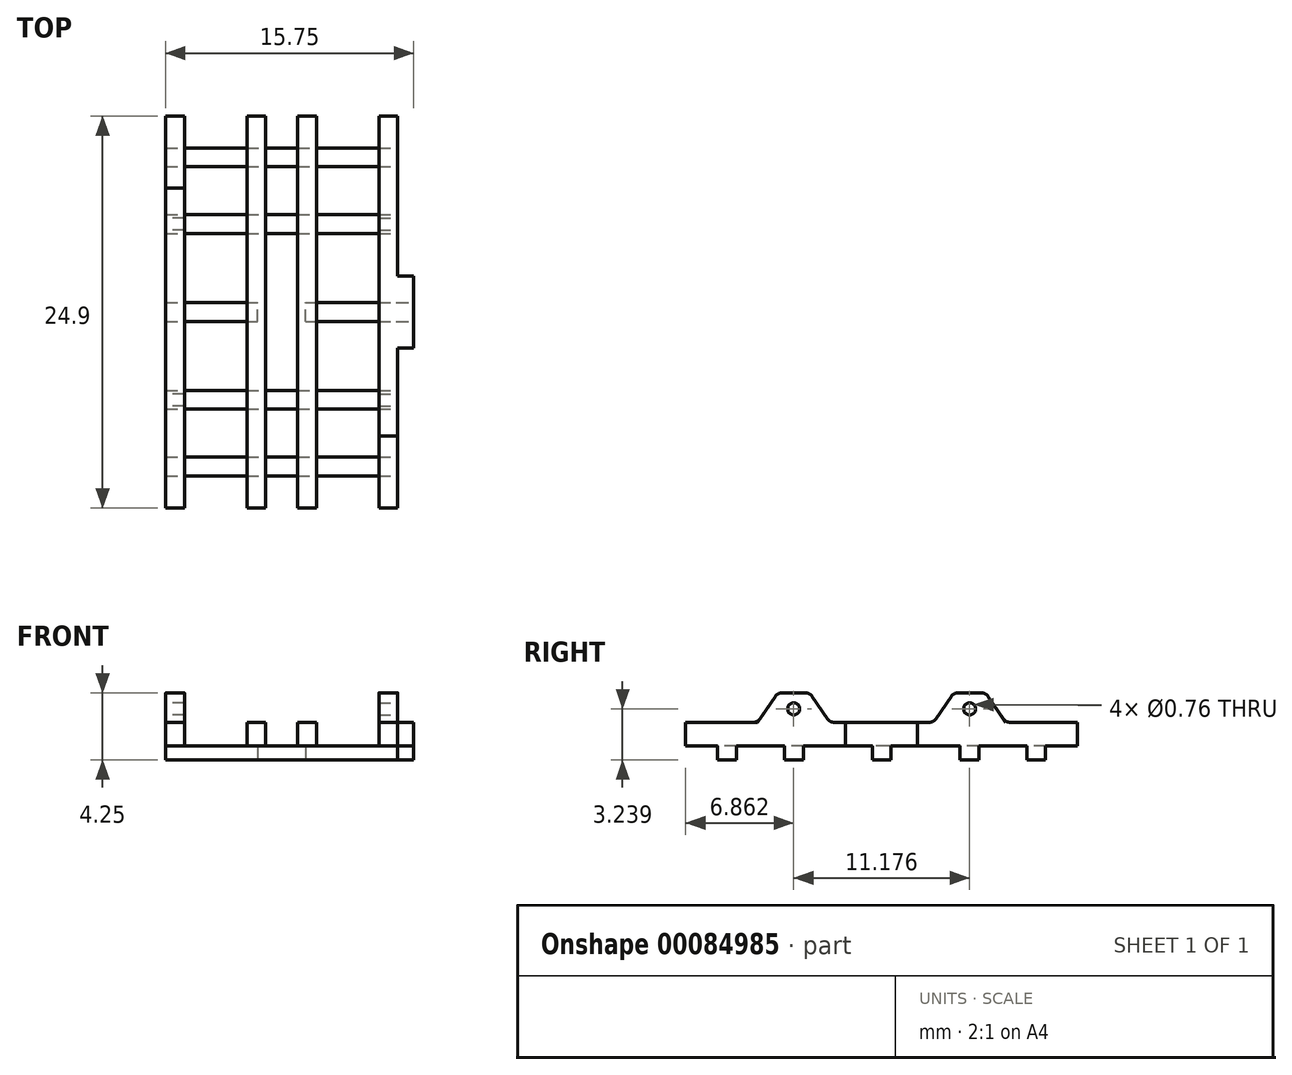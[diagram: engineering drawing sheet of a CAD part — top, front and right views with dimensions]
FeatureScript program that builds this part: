
annotation { "Feature Type Name" : "Feature", "Feature Type Description" : "" }
export const myFeature = defineFeature(function(context is Context, id is Id, definition is map)
    precondition{}
    {
        {
            var Q0;
            Q0=qCreatedBy(makeId("Top.planeOp"),FACE);
            var sketch = newSketch(context, id + "F0", { "sketchPlane" : qUnion([Q0])});
            skLineSegment(sketch, "E0.bottom", {"start": v(-7.37, 10.41) * mm, "end": v(7.37, 10.41) * mm});
            skLineSegment(sketch, "E0.top", {"start": v(-7.37, -10.41) * mm, "end": v(7.37, -10.41) * mm});
            skLineSegment(sketch, "E0.left", {"start": v(-7.37, 10.41) * mm, "end": v(-7.37, 9.22) * mm});
            skLineSegment(sketch, "E0.right", {"start": v(7.37, 10.41) * mm, "end": v(7.37, 9.22) * mm});
            skLineSegment(sketch, "E1", {"start": v(-7.37, 9.22) * mm, "end": v(7.37, 9.22) * mm});
            skLineSegment(sketch, "E2", {"start": v(-7.37, -9.22) * mm, "end": v(7.37, -9.22) * mm});
            skLineSegment(sketch, "E3", {"start": v(-7.37, -6.17) * mm, "end": v(7.37, -6.17) * mm});
            skLineSegment(sketch, "E4", {"start": v(-7.37, -4.98) * mm, "end": v(7.37, -4.98) * mm});
            skLineSegment(sketch, "E5", {"start": v(-7.37, -0.6) * mm, "end": v(7.37, -0.6) * mm});
            skLineSegment(sketch, "E6", {"start": v(-7.37, 0.6) * mm, "end": v(7.37, 0.6) * mm});
            skLineSegment(sketch, "E7", {"start": v(-7.37, 6.17) * mm, "end": v(7.37, 6.17) * mm});
            skLineSegment(sketch, "E8", {"start": v(-7.37, 4.98) * mm, "end": v(7.37, 4.98) * mm});
            skLineSegment(sketch, "E9.trimOffspring", {"start": v(-7.37, 6.17) * mm, "end": v(-7.37, 4.98) * mm});
            skLineSegment(sketch, "E10.trimOffspring", {"start": v(7.37, 6.17) * mm, "end": v(7.37, 4.98) * mm});
            skLineSegment(sketch, "E11.trimOffspring", {"start": v(-7.37, 0.6) * mm, "end": v(-7.37, -0.6) * mm});
            skLineSegment(sketch, "E12.trimOffspring", {"start": v(7.37, 0.6) * mm, "end": v(7.37, -0.6) * mm});
            skLineSegment(sketch, "E13.trimOffspring", {"start": v(-7.37, -4.98) * mm, "end": v(-7.37, -6.17) * mm});
            skLineSegment(sketch, "E14.trimOffspring", {"start": v(7.37, -4.98) * mm, "end": v(7.37, -6.17) * mm});
            skLineSegment(sketch, "E15.trimOffspring", {"start": v(7.37, -9.22) * mm, "end": v(7.37, -10.41) * mm});
            skLineSegment(sketch, "E16.trimOffspring", {"start": v(-7.37, -9.22) * mm, "end": v(-7.37, -10.41) * mm});
            skSolve(sketch);
        }
        {
            var Q0;
            Q0 = qSketchRegion(id + "F0", true);
            extrude(context, id + "F1", {"entities" : qUnion([Q0]), "depth" : 0.89 * mm});
        }
        {
            var Q0;
            Q0=makeQuery(id+"F1.opExtrude","CAP_FACE",FACE,{"disambiguationData":[OSD([sQuery(id+"F0.wireOp",EDGE,"E0.bottom"),sQuery(id+"F0.wireOp",EDGE,"E0.left"),sQuery(id+"F0.wireOp",EDGE,"E0.right"),sQuery(id+"F0.wireOp",EDGE,"E1")])],"isStart":false});
            var sketch = newSketch(context, id + "F2", { "sketchPlane" : qUnion([Q0])});
            skLineSegment(sketch, "E17.bottom", {"start": v(-7.37, 12.45) * mm, "end": v(-6.17, 12.45) * mm});
            skLineSegment(sketch, "E17.top", {"start": v(-7.37, -12.45) * mm, "end": v(-6.17, -12.45) * mm});
            skLineSegment(sketch, "E17.left", {"start": v(-7.37, 12.45) * mm, "end": v(-7.37, -12.45) * mm});
            skLineSegment(sketch, "E17.right", {"start": v(-6.17, 12.45) * mm, "end": v(-6.17, -12.45) * mm});
            skLineSegment(sketch, "E18.bottom", {"start": v(7.37, 12.45) * mm, "end": v(6.17, 12.45) * mm});
            skLineSegment(sketch, "E18.top", {"start": v(7.37, -12.45) * mm, "end": v(6.17, -12.45) * mm});
            skLineSegment(sketch, "E18.left", {"start": v(7.37, 12.45) * mm, "end": v(7.37, -12.45) * mm});
            skLineSegment(sketch, "E18.right", {"start": v(6.17, 12.45) * mm, "end": v(6.17, -12.45) * mm});
            skLineSegment(sketch, "E19.bottom", {"start": v(-2.2, 12.45) * mm, "end": v(-1.02, 12.45) * mm});
            skLineSegment(sketch, "E19.top", {"start": v(-2.2, -12.45) * mm, "end": v(-1.02, -12.45) * mm});
            skLineSegment(sketch, "E19.left", {"start": v(-2.2, 12.45) * mm, "end": v(-2.2, -12.45) * mm});
            skLineSegment(sketch, "E19.right", {"start": v(-1.02, 12.45) * mm, "end": v(-1.02, -12.45) * mm});
            skLineSegment(sketch, "E20.bottom", {"start": v(1.02, 12.45) * mm, "end": v(2.2, 12.45) * mm});
            skLineSegment(sketch, "E20.top", {"start": v(1.02, -12.45) * mm, "end": v(2.2, -12.45) * mm});
            skLineSegment(sketch, "E20.left", {"start": v(1.02, 12.45) * mm, "end": v(1.02, -12.45) * mm});
            skLineSegment(sketch, "E20.right", {"start": v(2.2, 12.45) * mm, "end": v(2.2, -12.45) * mm});
            skSolve(sketch);
        }
        {
            var Q0;
            Q0 = qSketchRegion(id + "F2", true);
            extrude(context, id + "F3", {"entities" : qUnion([Q0]), "operationType" : NewBodyOperationType.ADD, "depth" : 1.5 * mm});
        }
        {
            var Q0;
            Q0=makeQuery(id+"F3.boolean.opBoolean","MERGE",FACE,{"derivedFrom":[makeQuery(id+"F1.opExtrude","SWEPT_FACE",FACE,{"disambiguationData":[OSD([sQuery(id+"F0.wireOp",EDGE,"E0.left")])]}),makeQuery(id+"F1.opExtrude","SWEPT_FACE",FACE,{"disambiguationData":[OSD([sQuery(id+"F0.wireOp",EDGE,"E9.trimOffspring")])]}),makeQuery(id+"F1.opExtrude","SWEPT_FACE",FACE,{"disambiguationData":[OSD([sQuery(id+"F0.wireOp",EDGE,"E11.trimOffspring")])]}),makeQuery(id+"F1.opExtrude","SWEPT_FACE",FACE,{"disambiguationData":[OSD([sQuery(id+"F0.wireOp",EDGE,"E13.trimOffspring")])]}),makeQuery(id+"F1.opExtrude","SWEPT_FACE",FACE,{"disambiguationData":[OSD([sQuery(id+"F0.wireOp",EDGE,"E16.trimOffspring")])]}),makeQuery(id+"F3.opExtrude","SWEPT_FACE",FACE,{"disambiguationData":[OSD([sQuery(id+"F2.wireOp",EDGE,"E17.left")])]})]});
            var sketch = newSketch(context, id + "F4", { "sketchPlane" : qUnion([Q0])});
            skLineSegment(sketch, "E21", {"start": v(-7.87, 2.39) * mm, "end": v(-6.6, 4.25) * mm});
            skLineSegment(sketch, "E22", {"start": v(-6.6, 4.25) * mm, "end": v(-4.57, 4.25) * mm});
            skLineSegment(sketch, "E23", {"start": v(-4.57, 4.25) * mm, "end": v(-3.3, 2.39) * mm});
            skLineSegment(sketch, "E24", {"start": v(-3.3, 2.39) * mm, "end": v(-7.87, 2.39) * mm});
            skCircle(sketch, "E25", {"center": v(-5.59, 3.24) * mm, "radius": 0.38 * mm});
            skPoint(sketch, "E25.centerSnap0", {"position": v(-5.59, 4.25) * mm});
            skLineSegment(sketch, "E26.MirrorCS", {"start": v(3.3, 2.39) * mm, "end": v(7.87, 2.39) * mm});
            skLineSegment(sketch, "E27.MirrorCS", {"start": v(4.57, 4.25) * mm, "end": v(3.3, 2.39) * mm});
            skCircle(sketch, "E28.MirrorC", {"center": v(5.59, 3.24) * mm, "radius": 0.38 * mm});
            skLineSegment(sketch, "E29.MirrorCS", {"start": v(6.6, 4.25) * mm, "end": v(4.57, 4.25) * mm});
            skPoint(sketch, "E30.MirrorP", {"position": v(5.59, 4.25) * mm});
            skLineSegment(sketch, "E31.MirrorCS", {"start": v(7.87, 2.39) * mm, "end": v(6.6, 4.25) * mm});
            skSolve(sketch);
        }
        {
            var Q0;
            Q0 = qSketchRegion(id + "F4", true);
            extrude(context, id + "F5", {"entities" : qUnion([Q0]), "operationType" : NewBodyOperationType.ADD, "oppositeDirection" : true, "depth" : 1.2 * mm});
        }
        {
            var Q0;
            Q0=makeQuery(id+"F3.boolean.opBoolean","MERGE",FACE,{"derivedFrom":[makeQuery(id+"F1.opExtrude","SWEPT_FACE",FACE,{"disambiguationData":[OSD([sQuery(id+"F0.wireOp",EDGE,"E0.right")])]}),makeQuery(id+"F1.opExtrude","SWEPT_FACE",FACE,{"disambiguationData":[OSD([sQuery(id+"F0.wireOp",EDGE,"E10.trimOffspring")])]}),makeQuery(id+"F1.opExtrude","SWEPT_FACE",FACE,{"disambiguationData":[OSD([sQuery(id+"F0.wireOp",EDGE,"E12.trimOffspring")])]}),makeQuery(id+"F1.opExtrude","SWEPT_FACE",FACE,{"disambiguationData":[OSD([sQuery(id+"F0.wireOp",EDGE,"E14.trimOffspring")])]}),makeQuery(id+"F1.opExtrude","SWEPT_FACE",FACE,{"disambiguationData":[OSD([sQuery(id+"F0.wireOp",EDGE,"E15.trimOffspring")])]}),makeQuery(id+"F3.opExtrude","SWEPT_FACE",FACE,{"disambiguationData":[OSD([sQuery(id+"F2.wireOp",EDGE,"E18.left")])]})]});
            var sketch = newSketch(context, id + "F6", { "sketchPlane" : qUnion([Q0])});
            skLineSegment(sketch, "E32", {"start": v(-7.87, 2.39) * mm, "end": v(-3.3, 2.39) * mm});
            skLineSegment(sketch, "E33", {"start": v(-3.3, 2.39) * mm, "end": v(-4.57, 4.25) * mm});
            skLineSegment(sketch, "E34", {"start": v(-4.57, 4.25) * mm, "end": v(-6.6, 4.25) * mm});
            skLineSegment(sketch, "E35", {"start": v(-6.6, 4.25) * mm, "end": v(-7.87, 2.39) * mm});
            skCircle(sketch, "E36", {"center": v(-5.59, 3.24) * mm, "radius": 0.38 * mm});
            skLineSegment(sketch, "E37.MirrorCS", {"start": v(7.87, 2.39) * mm, "end": v(3.3, 2.39) * mm});
            skLineSegment(sketch, "E38.MirrorCS", {"start": v(3.3, 2.39) * mm, "end": v(4.57, 4.25) * mm});
            skLineSegment(sketch, "E39.MirrorCS", {"start": v(4.57, 4.25) * mm, "end": v(6.6, 4.25) * mm});
            skCircle(sketch, "E40.MirrorC", {"center": v(5.59, 3.24) * mm, "radius": 0.38 * mm});
            skLineSegment(sketch, "E41.MirrorCS", {"start": v(6.6, 4.25) * mm, "end": v(7.87, 2.39) * mm});
            skSolve(sketch);
        }
        {
            var Q0;
            Q0 = qSketchRegion(id + "F6", true);
            extrude(context, id + "F7", {"entities" : qUnion([Q0]), "operationType" : NewBodyOperationType.ADD, "oppositeDirection" : true, "depth" : 1.2 * mm});
        }
        {
            var Q0;
            Q0=makeQuery(id+"F7.opExtrude","SWEPT_EDGE",EDGE,{"disambiguationData":[OSD([sQuery(id+"F6.wireOp",EDGE,"E33"),sQuery(id+"F6.wireOp",EDGE,"E34")])]});
            var Q1;
            Q1=makeQuery(id+"F7.opExtrude","SWEPT_EDGE",EDGE,{"disambiguationData":[OSD([sQuery(id+"F6.wireOp",EDGE,"E34"),sQuery(id+"F6.wireOp",EDGE,"E35")])]});
            var Q2;
            Q2=makeQuery(id+"F7.opExtrude","SWEPT_EDGE",EDGE,{"disambiguationData":[OSD([sQuery(id+"F2.wireOp",EDGE,"E18.left"),sQuery(id+"F6.wireOp",EDGE,"E32"),sQuery(id+"F6.wireOp",EDGE,"E33")])]});
            var Q3;
            Q3=makeQuery(id+"F7.opExtrude","SWEPT_EDGE",EDGE,{"disambiguationData":[OSD([sQuery(id+"F2.wireOp",EDGE,"E18.left"),sQuery(id+"F6.wireOp",EDGE,"E32"),sQuery(id+"F6.wireOp",EDGE,"E35")])]});
            var Q4;
            Q4=makeQuery(id+"F7.opExtrude","SWEPT_EDGE",EDGE,{"disambiguationData":[OSD([sQuery(id+"F6.wireOp",EDGE,"E38.MirrorCS"),sQuery(id+"F6.wireOp",EDGE,"E39.MirrorCS")])]});
            var Q5;
            Q5=makeQuery(id+"F7.opExtrude","SWEPT_EDGE",EDGE,{"disambiguationData":[OSD([sQuery(id+"F2.wireOp",EDGE,"E18.left"),sQuery(id+"F6.wireOp",EDGE,"E37.MirrorCS"),sQuery(id+"F6.wireOp",EDGE,"E38.MirrorCS")])]});
            var Q6;
            Q6=makeQuery(id+"F7.opExtrude","SWEPT_EDGE",EDGE,{"disambiguationData":[OSD([sQuery(id+"F6.wireOp",EDGE,"E39.MirrorCS"),sQuery(id+"F6.wireOp",EDGE,"E41.MirrorCS")])]});
            var Q7;
            Q7=makeQuery(id+"F7.opExtrude","SWEPT_EDGE",EDGE,{"disambiguationData":[OSD([sQuery(id+"F2.wireOp",EDGE,"E18.left"),sQuery(id+"F6.wireOp",EDGE,"E37.MirrorCS"),sQuery(id+"F6.wireOp",EDGE,"E41.MirrorCS")])]});
            var Q8;
            Q8=makeQuery(id+"F5.opExtrude","SWEPT_EDGE",EDGE,{"disambiguationData":[OSD([sQuery(id+"F2.wireOp",EDGE,"E17.left"),sQuery(id+"F4.wireOp",EDGE,"E21"),sQuery(id+"F4.wireOp",EDGE,"E24")])]});
            var Q9;
            Q9=makeQuery(id+"F5.opExtrude","SWEPT_EDGE",EDGE,{"disambiguationData":[OSD([sQuery(id+"F4.wireOp",EDGE,"E21"),sQuery(id+"F4.wireOp",EDGE,"E22")])]});
            var Q10;
            Q10=makeQuery(id+"F5.opExtrude","SWEPT_EDGE",EDGE,{"disambiguationData":[OSD([sQuery(id+"F4.wireOp",EDGE,"E22"),sQuery(id+"F4.wireOp",EDGE,"E23")])]});
            var Q11;
            Q11=makeQuery(id+"F5.opExtrude","SWEPT_EDGE",EDGE,{"disambiguationData":[OSD([sQuery(id+"F2.wireOp",EDGE,"E17.left"),sQuery(id+"F4.wireOp",EDGE,"E23"),sQuery(id+"F4.wireOp",EDGE,"E24")])]});
            var Q12;
            Q12=makeQuery(id+"F5.opExtrude","SWEPT_EDGE",EDGE,{"disambiguationData":[OSD([sQuery(id+"F2.wireOp",EDGE,"E17.left"),sQuery(id+"F4.wireOp",EDGE,"E26.MirrorCS"),sQuery(id+"F4.wireOp",EDGE,"E31.MirrorCS")])]});
            var Q13;
            Q13=makeQuery(id+"F5.opExtrude","SWEPT_EDGE",EDGE,{"disambiguationData":[OSD([sQuery(id+"F4.wireOp",EDGE,"E29.MirrorCS"),sQuery(id+"F4.wireOp",EDGE,"E31.MirrorCS")])]});
            var Q14;
            Q14=makeQuery(id+"F5.opExtrude","SWEPT_EDGE",EDGE,{"disambiguationData":[OSD([sQuery(id+"F4.wireOp",EDGE,"E27.MirrorCS"),sQuery(id+"F4.wireOp",EDGE,"E29.MirrorCS")])]});
            var Q15;
            Q15=makeQuery(id+"F5.opExtrude","SWEPT_EDGE",EDGE,{"disambiguationData":[OSD([sQuery(id+"F2.wireOp",EDGE,"E17.left"),sQuery(id+"F4.wireOp",EDGE,"E26.MirrorCS"),sQuery(id+"F4.wireOp",EDGE,"E27.MirrorCS")])]});
            fillet(context, id + "F8", {"entities" : qUnion([Q0, Q1, Q2, Q3, Q4, Q5, Q6, Q7, Q8, Q9, Q10, Q11, Q12, Q13, Q14, Q15]), "radius" : 0.5 * mm, "tangentPropagation" : true, "allowEdgeOverflow" : false});
        }
        {
            var Q0;
            Q0=makeQuery(id+"F1.opExtrude","CAP_FACE",FACE,{"disambiguationData":[OSD([sQuery(id+"F0.wireOp",EDGE,"E5"),sQuery(id+"F0.wireOp",EDGE,"E6"),sQuery(id+"F0.wireOp",EDGE,"E11.trimOffspring"),sQuery(id+"F0.wireOp",EDGE,"E12.trimOffspring")])],"isStart":true});
            var sketch = newSketch(context, id + "F9", { "sketchPlane" : qUnion([Q0])});
            skLineSegment(sketch, "E42.bottom", {"start": v(-1.52, 0.6) * mm, "end": v(1.52, 0.6) * mm});
            skLineSegment(sketch, "E42.top", {"start": v(-1.52, -0.6) * mm, "end": v(1.52, -0.6) * mm});
            skLineSegment(sketch, "E42.left", {"start": v(-1.52, 0.6) * mm, "end": v(-1.52, -0.6) * mm});
            skLineSegment(sketch, "E42.right", {"start": v(1.52, 0.6) * mm, "end": v(1.52, -0.6) * mm});
            skSolve(sketch);
        }
        {
            var Q0;
            Q0 = qSketchRegion(id + "F9", true);
            var Q1;
            {var subQ1=sQuery(id+"F2.wireOp",EDGE,"E19.left");var subQ2=sQuery(id+"F0.wireOp",EDGE,"E6");var subQ3=sQuery(id+"F2.wireOp",EDGE,"E19.right");Q1=makeQuery(id+"F3.boolean.opBoolean","SPLIT",FACE,{"disambiguationData":[TD([makeQuery(id+"F1.opExtrude","SWEPT_FACE",FACE,{"disambiguationData":[OSD([subQ2])]})])],"derivedFrom":makeQuery(id+"F3.opExtrude","CAP_FACE",FACE,{"disambiguationData":[OSD([sQuery(id+"F2.wireOp",EDGE,"E19.bottom"),sQuery(id+"F2.wireOp",EDGE,"E19.top"),subQ1,subQ3])],"isStart":true})});}
            extrude(context, id + "F10", {"entities" : qUnion([Q0]), "operationType" : NewBodyOperationType.REMOVE, "endBound" : BoundingType.UP_TO_SURFACE, "oppositeDirection" : true, "endBoundEntityFace" : qUnion([Q1]), "depth" : 25.4 * mm});
        }
        {
            var Q0;
            {var subQ0=sQuery(id+"F0.wireOp",EDGE,"E6");var subQ1=sQuery(id+"F0.wireOp",EDGE,"E12.trimOffspring");var subQ2=sQuery(id+"F0.wireOp",EDGE,"E5");Q0=makeQuery(id+"F10.boolean.opBoolean","SPLIT",FACE,{"disambiguationData":[TD([makeQuery(id+"F1.opExtrude","SWEPT_FACE",FACE,{"disambiguationData":[OSD([sQuery(id+"F0.wireOp",EDGE,"E0.right")])]})])],"derivedFrom":makeQuery(id+"F1.opExtrude","CAP_FACE",FACE,{"disambiguationData":[OSD([subQ2,subQ0,sQuery(id+"F0.wireOp",EDGE,"E11.trimOffspring"),subQ1])],"isStart":true})});}
            var sketch = newSketch(context, id + "F11", { "sketchPlane" : qUnion([Q0])});
            skLineSegment(sketch, "E43.bottom", {"start": v(7.37, 0.6) * mm, "end": v(8.38, 0.6) * mm});
            skLineSegment(sketch, "E43.top", {"start": v(7.37, -0.6) * mm, "end": v(8.38, -0.6) * mm});
            skLineSegment(sketch, "E43.left", {"start": v(7.37, 0.6) * mm, "end": v(7.37, -0.6) * mm});
            skLineSegment(sketch, "E43.right", {"start": v(8.38, 0.6) * mm, "end": v(8.38, -0.6) * mm});
            skSolve(sketch);
        }
        {
            var Q0;
            Q0 = qSketchRegion(id + "F11", true);
            var Q1;
            {var subQ0=sQuery(id+"F6.wireOp",EDGE,"E33");var subQ5=sQuery(id+"F2.wireOp",EDGE,"E18.right");var subQ6=sQuery(id+"F2.wireOp",EDGE,"E18.left");Q1=makeQuery(id+"F7.boolean.opBoolean","SPLIT",FACE,{"disambiguationData":[TD([makeQuery(id+"F7.opExtrude","SWEPT_FACE",FACE,{"disambiguationData":[OSD([subQ0])]})])],"derivedFrom":makeQuery(id+"F3.opExtrude","CAP_FACE",FACE,{"disambiguationData":[OSD([sQuery(id+"F2.wireOp",EDGE,"E18.bottom"),sQuery(id+"F2.wireOp",EDGE,"E18.top"),subQ6,subQ5])],"isStart":false})});}
            extrude(context, id + "F12", {"entities" : qUnion([Q0]), "operationType" : NewBodyOperationType.ADD, "endBound" : BoundingType.UP_TO_SURFACE, "oppositeDirection" : true, "endBoundEntityFace" : qUnion([Q1]), "depth" : 25.4 * mm});
        }
        {
            var Q0;
            Q0=makeQuery(id+"F12.opExtrude","SWEPT_FACE",FACE,{"disambiguationData":[OSD([sQuery(id+"F11.wireOp",EDGE,"E43.right")])]});
            var sketch = newSketch(context, id + "F13", { "sketchPlane" : qUnion([Q0])});
            skLineSegment(sketch, "E44.bottom", {"start": v(-2.29, 2.39) * mm, "end": v(2.29, 2.39) * mm});
            skLineSegment(sketch, "E44.top", {"start": v(-2.29, 0.89) * mm, "end": v(2.29, 0.89) * mm});
            skLineSegment(sketch, "E44.left", {"start": v(-2.29, 2.39) * mm, "end": v(-2.29, 0.89) * mm});
            skLineSegment(sketch, "E44.right", {"start": v(2.29, 2.39) * mm, "end": v(2.29, 0.89) * mm});
            skSolve(sketch);
        }
        {
            var Q0;
            Q0 = qSketchRegion(id + "F13", true);
            var Q1;
            {var subQ1=sQuery(id+"F2.wireOp",EDGE,"E18.left");var subQ4=sQuery(id+"F0.wireOp",EDGE,"E0.bottom");var subQ6=sQuery(id+"F0.wireOp",EDGE,"E10.trimOffspring");var subQ9=sQuery(id+"F0.wireOp",EDGE,"E0.right");var subQ10=sQuery(id+"F6.wireOp",EDGE,"E41.MirrorCS");var subQ11=sQuery(id+"F6.wireOp",EDGE,"E39.MirrorCS");var subQ12=sQuery(id+"F6.wireOp",EDGE,"E38.MirrorCS");var subQ13=sQuery(id+"F6.wireOp",EDGE,"E37.MirrorCS");var subQ14=sQuery(id+"F6.wireOp",EDGE,"E40.MirrorC");Q1=makeQuery(id+"F12.boolean.opBoolean","SPLIT",FACE,{"disambiguationData":[TD([makeQuery(id+"F1.opExtrude","SWEPT_FACE",FACE,{"disambiguationData":[OSD([subQ4])]})])],"derivedFrom":makeQuery(id+"F7.boolean.opBoolean","MERGE",FACE,{"derivedFrom":[makeQuery(id+"F3.boolean.opBoolean","MERGE",FACE,{"derivedFrom":[makeQuery(id+"F1.opExtrude","SWEPT_FACE",FACE,{"disambiguationData":[OSD([subQ9])]}),makeQuery(id+"F1.opExtrude","SWEPT_FACE",FACE,{"disambiguationData":[OSD([subQ6])]}),makeQuery(id+"F1.opExtrude","SWEPT_FACE",FACE,{"disambiguationData":[OSD([sQuery(id+"F0.wireOp",EDGE,"E12.trimOffspring")])]}),makeQuery(id+"F1.opExtrude","SWEPT_FACE",FACE,{"disambiguationData":[OSD([sQuery(id+"F0.wireOp",EDGE,"E14.trimOffspring")])]}),makeQuery(id+"F1.opExtrude","SWEPT_FACE",FACE,{"disambiguationData":[OSD([sQuery(id+"F0.wireOp",EDGE,"E15.trimOffspring")])]}),makeQuery(id+"F3.opExtrude","SWEPT_FACE",FACE,{"disambiguationData":[OSD([subQ1])]})]}),makeQuery(id+"F7.opExtrude","CAP_FACE",FACE,{"disambiguationData":[OSD([sQuery(id+"F6.wireOp",EDGE,"E32"),sQuery(id+"F6.wireOp",EDGE,"E33"),sQuery(id+"F6.wireOp",EDGE,"E34"),sQuery(id+"F6.wireOp",EDGE,"E35"),sQuery(id+"F6.wireOp",EDGE,"E36")])],"isStart":true}),makeQuery(id+"F7.opExtrude","CAP_FACE",FACE,{"disambiguationData":[OSD([subQ13,subQ12,subQ11,subQ14,subQ10])],"isStart":true})]})});}
            var Q2;
            Q2=makeQuery(id+"F1.opExtrude","SWEPT_BODY",BODY,{"disambiguationData":[OSD([sQuery(id+"F0.wireOp",EDGE,"E0.bottom"),sQuery(id+"F0.wireOp",EDGE,"E0.left"),sQuery(id+"F0.wireOp",EDGE,"E0.right"),sQuery(id+"F0.wireOp",EDGE,"E1")])]});
            extrude(context, id + "F14", {"entities" : qUnion([Q0]), "operationType" : NewBodyOperationType.ADD, "endBound" : BoundingType.UP_TO_SURFACE, "oppositeDirection" : true, "endBoundEntityFace" : qUnion([Q1]), "endBoundEntityBody" : qUnion([Q2]), "depth" : 25.4 * mm});
        }
    });
